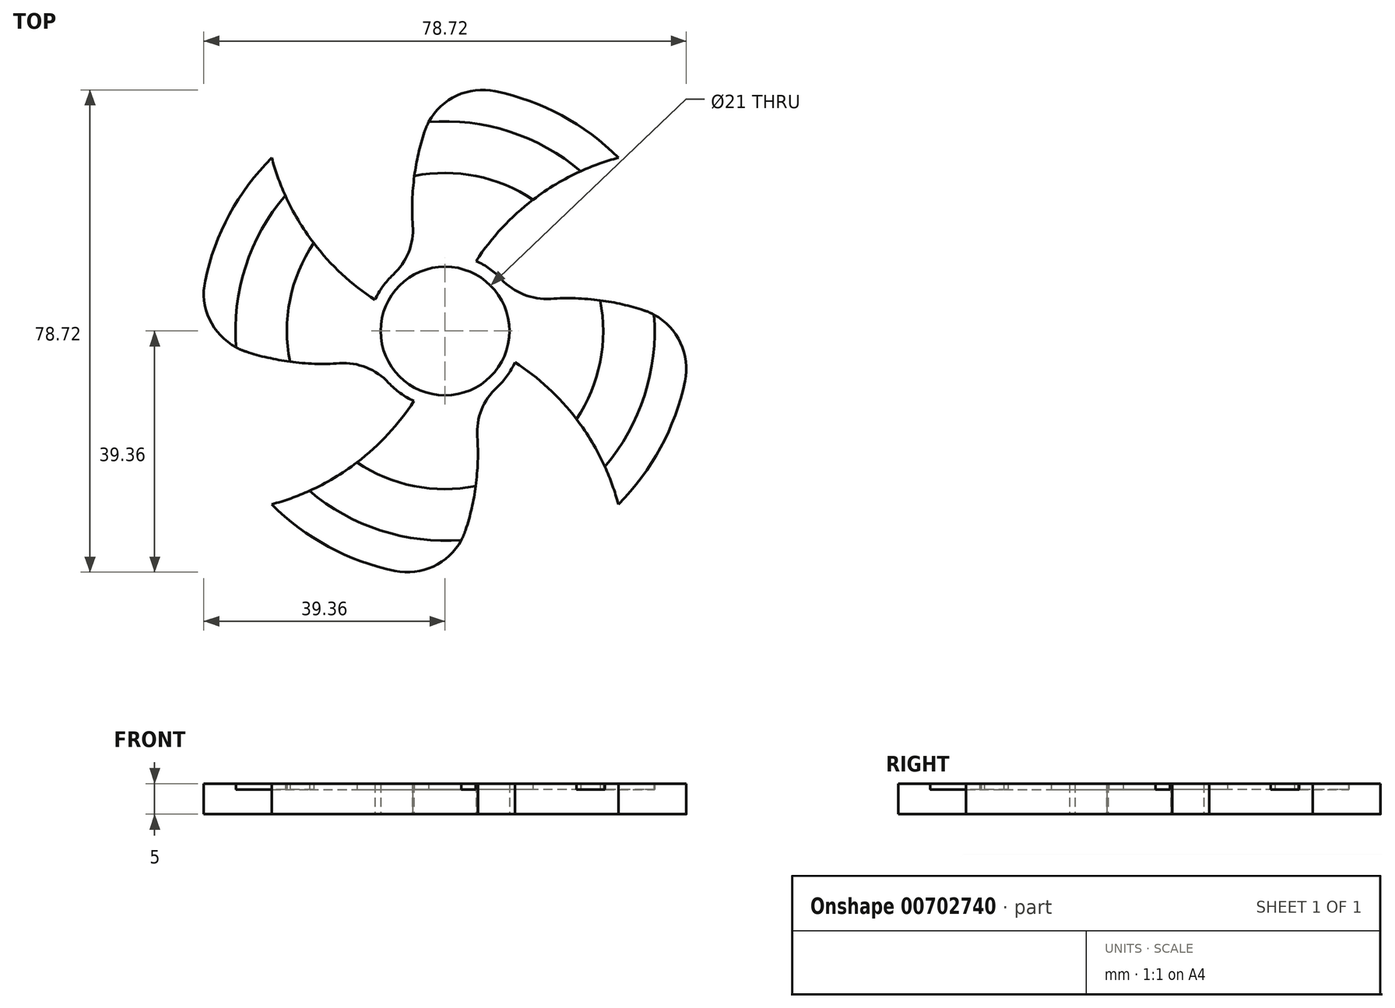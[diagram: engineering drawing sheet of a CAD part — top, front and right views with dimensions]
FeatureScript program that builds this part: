
annotation { "Feature Type Name" : "Feature", "Feature Type Description" : "" }
export const myFeature = defineFeature(function(context is Context, id is Id, definition is map)
    precondition{}
    {
        {
            var Q0;
            Q0=qCreatedBy(makeId("Top.planeOp"),FACE);
            var sketch = newSketch(context, id + "F0", { "sketchPlane" : qUnion([Q0])});
            skArc(sketch, "E0", {"start": v(28.28, 28.28) * mm, "mid": v(15.3, 36.96) * mm, "end": v(0, 40) * mm});
            skLineSegment(sketch, "E1", {"start": v(0, 0) * mm, "end": v(40, 0) * mm, "construction": true});
            skLineSegment(sketch, "E2", {"start": v(0, 0) * mm, "end": v(-40, 0) * mm, "construction": true});
            skLineSegment(sketch, "E3", {"start": v(0, 0) * mm, "end": v(-28.28, 28.28) * mm, "construction": true});
            skLineSegment(sketch, "E4", {"start": v(0, 0) * mm, "end": v(28.28, 28.28) * mm, "construction": true});
            skLineSegment(sketch, "E5", {"start": v(0, 0) * mm, "end": v(28.28, -28.28) * mm, "construction": true});
            skLineSegment(sketch, "E6", {"start": v(0, 0) * mm, "end": v(-28.28, -28.28) * mm, "construction": true});
            skLineSegment(sketch, "E7", {"start": v(0, 40) * mm, "end": v(0, -40) * mm, "construction": true});
            skArc(sketch, "E8", {"start": v(28.28, 28.28) * mm, "mid": v(15.12, 22) * mm, "end": v(5.08, 11.42) * mm});
            skArc(sketch, "E9", {"start": v(40, 0) * mm, "mid": v(26.25, 4.87) * mm, "end": v(11.67, 4.48) * mm});
            skArc(sketch, "E10", {"start": v(28.28, -28.28) * mm, "mid": v(22, -15.12) * mm, "end": v(11.42, -5.08) * mm});
            skArc(sketch, "E11", {"start": v(0, -40) * mm, "mid": v(4.87, -26.25) * mm, "end": v(4.48, -11.67) * mm});
            skArc(sketch, "E12", {"start": v(-28.28, -28.28) * mm, "mid": v(-15.12, -22) * mm, "end": v(-5.08, -11.42) * mm});
            skArc(sketch, "E13", {"start": v(-40, 0) * mm, "mid": v(-26.25, -4.87) * mm, "end": v(-11.67, -4.48) * mm});
            skArc(sketch, "E14", {"start": v(-28.28, 28.28) * mm, "mid": v(-22, 15.12) * mm, "end": v(-11.42, 5.08) * mm});
            skArc(sketch, "E15", {"start": v(0, 40) * mm, "mid": v(-4.87, 26.25) * mm, "end": v(-4.48, 11.67) * mm});
            skArc(sketch, "E16.trimOffspring", {"start": v(-28.28, -28.28) * mm, "mid": v(-15.3, -36.96) * mm, "end": v(0, -40) * mm});
            skArc(sketch, "E17.trimOffspring", {"start": v(28.28, -28.28) * mm, "mid": v(36.96, -15.3) * mm, "end": v(40, 0) * mm});
            skArc(sketch, "E18.trimOffspring", {"start": v(-28.28, 28.28) * mm, "mid": v(-36.96, 15.3) * mm, "end": v(-40, 0) * mm});
            skCircle(sketch, "E19", {"center": v(0, 0) * mm, "radius": 12.5 * mm});
            skCircle(sketch, "E20", {"center": v(0, 0) * mm, "radius": 10.5 * mm});
            skSolve(sketch);
        }
        {
            var Q0;
            {var subQ0=sQuery(id+"F0.wireOp",EDGE,"E13");Q0=makeQuery(id+"F0.imprint","IMPRINT",FACE,{"disambiguationData":[TD([[makeQuery(id+"F0.imprint","IMPRINT",EDGE,{"derivedFrom":subQ0}),1.0]])]});}
            var Q1;
            Q1=makeQuery(id+"F0.imprint","IMPRINT",FACE,{"disambiguationData":[TD([[makeQuery(id+"F0.imprint","IMPRINT",EDGE,{"derivedFrom":sQuery(id+"F0.wireOp",EDGE,"E0")}),1.0]])]});
            var Q2;
            Q2=makeQuery(id+"F0.imprint","IMPRINT",FACE,{"disambiguationData":[TD([[makeQuery(id+"F0.imprint","IMPRINT",EDGE,{"derivedFrom":sQuery(id+"F0.wireOp",EDGE,"E20")}),-1.0]])]});
            var Q3;
            {var subQ0=sQuery(id+"F0.wireOp",EDGE,"E9");Q3=makeQuery(id+"F0.imprint","IMPRINT",FACE,{"disambiguationData":[TD([[makeQuery(id+"F0.imprint","IMPRINT",EDGE,{"derivedFrom":subQ0}),1.0]])]});}
            var Q4;
            {var subQ0=sQuery(id+"F0.wireOp",EDGE,"E11");Q4=makeQuery(id+"F0.imprint","IMPRINT",FACE,{"disambiguationData":[TD([[makeQuery(id+"F0.imprint","IMPRINT",EDGE,{"derivedFrom":subQ0}),1.0]])]});}
            extrude(context, id + "F1", {"entities" : qUnion([Q0, Q1, Q2, Q3, Q4]), "depth" : 5 * mm, "offsetDistance" : 25 * mm});
        }
        {
            var Q0;
            Q0=makeQuery(id+"F1.opExtrude","SWEPT_EDGE",EDGE,{"disambiguationData":[OSD([sQuery(id+"F0.wireOp",EDGE,"E13"),sQuery(id+"F0.wireOp",EDGE,"E18.trimOffspring")])]});
            var Q1;
            Q1=makeQuery(id+"F1.opExtrude","SWEPT_EDGE",EDGE,{"disambiguationData":[OSD([sQuery(id+"F0.wireOp",EDGE,"E11"),sQuery(id+"F0.wireOp",EDGE,"E16.trimOffspring")])]});
            var Q2;
            Q2=makeQuery(id+"F1.opExtrude","SWEPT_EDGE",EDGE,{"disambiguationData":[OSD([sQuery(id+"F0.wireOp",EDGE,"E9"),sQuery(id+"F0.wireOp",EDGE,"E17.trimOffspring")])]});
            var Q3;
            Q3=makeQuery(id+"F1.opExtrude","SWEPT_EDGE",EDGE,{"disambiguationData":[OSD([sQuery(id+"F0.wireOp",EDGE,"E0"),sQuery(id+"F0.wireOp",EDGE,"E15")])]});
            fillet(context, id + "F2", {"entities" : qUnion([Q0, Q1, Q2, Q3]), "radius" : 10 * mm, "tangentPropagation" : true, "allowEdgeOverflow" : false});
        }
        {
            var Q0;
            Q0=makeQuery(id+"F1.opExtrude","CAP_FACE",FACE,{"disambiguationData":[OSD([sQuery(id+"F0.wireOp",EDGE,"E0"),sQuery(id+"F0.wireOp",EDGE,"E8"),sQuery(id+"F0.wireOp",EDGE,"E9"),sQuery(id+"F0.wireOp",EDGE,"E10"),sQuery(id+"F0.wireOp",EDGE,"E11"),sQuery(id+"F0.wireOp",EDGE,"E12"),sQuery(id+"F0.wireOp",EDGE,"E13"),sQuery(id+"F0.wireOp",EDGE,"E14"),sQuery(id+"F0.wireOp",EDGE,"E15"),sQuery(id+"F0.wireOp",EDGE,"E16.trimOffspring"),sQuery(id+"F0.wireOp",EDGE,"E17.trimOffspring"),sQuery(id+"F0.wireOp",EDGE,"E18.trimOffspring"),sQuery(id+"F0.wireOp",EDGE,"E19"),sQuery(id+"F0.wireOp",EDGE,"E20")])],"isStart":false});
            var sketch = newSketch(context, id + "F3", { "sketchPlane" : qUnion([Q0])});
            skCircle(sketch, "E21", {"center": v(0, 0) * mm, "radius": 25.8 * mm});
            skCircle(sketch, "E22", {"center": v(0, 0) * mm, "radius": 34.2 * mm});
            skSolve(sketch);
        }
        {
            var Q0;
            {var subQ3=sQuery(id+"F0.wireOp",EDGE,"E14");var subQ8=makeQuery(id+"F1.opExtrude","CAP_EDGE",EDGE,{"disambiguationData":[OSD([subQ3])],"isStart":false});var subQ10=sQuery(id+"F3.wireOp",EDGE,"E21");var subQ11=makeQuery(id+"F3.imprint","INTERSECT",VERTEX,{"derivedFrom":[subQ8,subQ10]});Q0=makeQuery(id+"F3.imprint","IMPRINT",FACE,{"disambiguationData":[TD([[makeQuery(id+"F3.imprint","IMPRINT",EDGE,{"disambiguationData":[TD([[subQ11,-1.0]])],"derivedFrom":subQ10}),-1.0]])]});}
            var Q1;
            {var subQ2=sQuery(id+"F0.wireOp",EDGE,"E8");var subQ8=makeQuery(id+"F1.opExtrude","CAP_EDGE",EDGE,{"disambiguationData":[OSD([subQ2])],"isStart":false});var subQ10=sQuery(id+"F3.wireOp",EDGE,"E21");var subQ11=makeQuery(id+"F3.imprint","INTERSECT",VERTEX,{"derivedFrom":[subQ8,subQ10]});Q1=makeQuery(id+"F3.imprint","IMPRINT",FACE,{"disambiguationData":[TD([[makeQuery(id+"F3.imprint","IMPRINT",EDGE,{"disambiguationData":[TD([[subQ11,-1.0]])],"derivedFrom":subQ10}),-1.0]])]});}
            var Q2;
            {var subQ0=sQuery(id+"F0.wireOp",EDGE,"E9");var subQ1=makeQuery(id+"F1.opExtrude","CAP_EDGE",EDGE,{"disambiguationData":[OSD([subQ0])],"isStart":false});var subQ8=sQuery(id+"F3.wireOp",EDGE,"E21");var subQ9=makeQuery(id+"F3.imprint","INTERSECT",VERTEX,{"derivedFrom":[subQ1,subQ8]});Q2=makeQuery(id+"F3.imprint","IMPRINT",FACE,{"disambiguationData":[TD([[makeQuery(id+"F3.imprint","IMPRINT",EDGE,{"disambiguationData":[TD([[subQ9,1.0]])],"derivedFrom":subQ8}),-1.0]])]});}
            var Q3;
            {var subQ3=sQuery(id+"F0.wireOp",EDGE,"E12");var subQ8=makeQuery(id+"F1.opExtrude","CAP_EDGE",EDGE,{"disambiguationData":[OSD([subQ3])],"isStart":false});var subQ10=sQuery(id+"F3.wireOp",EDGE,"E21");var subQ11=makeQuery(id+"F3.imprint","INTERSECT",VERTEX,{"derivedFrom":[subQ8,subQ10]});Q3=makeQuery(id+"F3.imprint","IMPRINT",FACE,{"disambiguationData":[TD([[makeQuery(id+"F3.imprint","IMPRINT",EDGE,{"disambiguationData":[TD([[subQ11,-1.0]])],"derivedFrom":subQ10}),-1.0]])]});}
            extrude(context, id + "F4", {"entities" : qUnion([Q0, Q1, Q2, Q3]), "operationType" : NewBodyOperationType.REMOVE, "oppositeDirection" : true, "depth" : 1 * mm, "offsetDistance" : 25 * mm});
        }
        {
            var Q0;
            {var subQ0=sQuery(id+"F0.wireOp",EDGE,"E13");var subQ1=makeQuery(id+"F1.opExtrude","CAP_EDGE",EDGE,{"disambiguationData":[OSD([subQ0])],"isStart":false});var subQ2=sQuery(id+"F0.wireOp",EDGE,"E20");var subQ3=sQuery(id+"F0.wireOp",EDGE,"E19");var subQ4=sQuery(id+"F0.wireOp",EDGE,"E18.trimOffspring");var subQ5=sQuery(id+"F0.wireOp",EDGE,"E17.trimOffspring");var subQ6=sQuery(id+"F0.wireOp",EDGE,"E16.trimOffspring");var subQ7=sQuery(id+"F0.wireOp",EDGE,"E15");var subQ8=sQuery(id+"F0.wireOp",EDGE,"E14");var subQ9=sQuery(id+"F0.wireOp",EDGE,"E12");var subQ10=sQuery(id+"F0.wireOp",EDGE,"E11");var subQ11=sQuery(id+"F0.wireOp",EDGE,"E10");var subQ12=sQuery(id+"F0.wireOp",EDGE,"E9");var subQ13=sQuery(id+"F0.wireOp",EDGE,"E8");var subQ14=sQuery(id+"F0.wireOp",EDGE,"E0");var subQ15=makeQuery(id+"F2.opFillet","BLEND_EDGE",EDGE,{"blendedFrom":[makeQuery(id+"F1.opExtrude","SWEPT_EDGE",EDGE,{"disambiguationData":[OSD([subQ0,subQ4])]}),makeQuery(id+"F1.opExtrude","CAP_FACE",FACE,{"disambiguationData":[OSD([subQ14,subQ13,subQ12,subQ11,subQ10,subQ9,subQ0,subQ8,subQ7,subQ6,subQ5,subQ4,subQ3,subQ2])],"isStart":false})],"blendedInto":[makeQuery(id+"F1.opExtrude","CAP_FACE",FACE,{"disambiguationData":[OSD([subQ14,subQ13,subQ12,subQ11,subQ10,subQ9,subQ0,subQ8,subQ7,subQ6,subQ5,subQ4,subQ3,subQ2])],"isStart":false})]});var subQ16=makeQuery(id+"F3.imprint","INTERSECT",VERTEX,{"derivedFrom":[subQ15,subQ1]});var subQ17=sQuery(id+"F3.wireOp",EDGE,"E21");var subQ18=makeQuery(id+"F3.imprint","INTERSECT",VERTEX,{"derivedFrom":[subQ1,subQ17]});var subQ19=sQuery(id+"F3.wireOp",EDGE,"E22");var subQ21=makeQuery(id+"F1.opExtrude","CAP_EDGE",EDGE,{"disambiguationData":[OSD([subQ8])],"isStart":false});var subQ22=makeQuery(id+"F3.imprint","INTERSECT",VERTEX,{"derivedFrom":[subQ21,subQ19]});var subQ23=makeQuery(id+"F3.imprint","INTERSECT",VERTEX,{"derivedFrom":[subQ21,subQ17]});Q0=makeQuery(id+"F4.boolean.opBoolean","COPY",FACE,{"derivedFrom":makeQuery(id+"F4.opExtrude","CAP_FACE",FACE,{"disambiguationData":[OSD([subQ14,subQ13,subQ12,subQ11,subQ10,subQ9,subQ0,subQ8,subQ7,subQ6,subQ5,subQ4,subQ3,subQ2,subQ17,subQ19]),TDD([makeQuery(id+"F3.imprint","IMPRINT",EDGE,{"disambiguationData":[TD([[subQ23,-1.0]])],"derivedFrom":subQ17}),makeQuery(id+"F3.imprint","IMPRINT",EDGE,{"disambiguationData":[TD([[subQ22,-1.0]])],"derivedFrom":subQ19}),makeQuery(id+"F3.imprint","IMPRINT",EDGE,{"disambiguationData":[TD([[subQ22,-1.0]])],"derivedFrom":subQ21}),makeQuery(id+"F3.imprint","IMPRINT",EDGE,{"disambiguationData":[TD([[subQ16,1.0]])],"derivedFrom":subQ15}),makeQuery(id+"F3.imprint","IMPRINT",EDGE,{"disambiguationData":[TD([[subQ18,1.0]])],"derivedFrom":subQ1})])],"isStart":false})});}
            var Q1;
            {var subQ0=sQuery(id+"F0.wireOp",EDGE,"E15");var subQ1=makeQuery(id+"F1.opExtrude","CAP_EDGE",EDGE,{"disambiguationData":[OSD([subQ0])],"isStart":false});var subQ2=sQuery(id+"F0.wireOp",EDGE,"E20");var subQ3=sQuery(id+"F0.wireOp",EDGE,"E19");var subQ4=sQuery(id+"F0.wireOp",EDGE,"E18.trimOffspring");var subQ5=sQuery(id+"F0.wireOp",EDGE,"E17.trimOffspring");var subQ6=sQuery(id+"F0.wireOp",EDGE,"E16.trimOffspring");var subQ7=sQuery(id+"F0.wireOp",EDGE,"E14");var subQ8=sQuery(id+"F0.wireOp",EDGE,"E13");var subQ9=sQuery(id+"F0.wireOp",EDGE,"E12");var subQ10=sQuery(id+"F0.wireOp",EDGE,"E11");var subQ11=sQuery(id+"F0.wireOp",EDGE,"E10");var subQ12=sQuery(id+"F0.wireOp",EDGE,"E9");var subQ13=sQuery(id+"F0.wireOp",EDGE,"E8");var subQ14=sQuery(id+"F0.wireOp",EDGE,"E0");var subQ15=makeQuery(id+"F2.opFillet","BLEND_EDGE",EDGE,{"blendedFrom":[makeQuery(id+"F1.opExtrude","SWEPT_EDGE",EDGE,{"disambiguationData":[OSD([subQ14,subQ0])]}),makeQuery(id+"F1.opExtrude","CAP_FACE",FACE,{"disambiguationData":[OSD([subQ14,subQ13,subQ12,subQ11,subQ10,subQ9,subQ8,subQ7,subQ0,subQ6,subQ5,subQ4,subQ3,subQ2])],"isStart":false})],"blendedInto":[makeQuery(id+"F1.opExtrude","CAP_FACE",FACE,{"disambiguationData":[OSD([subQ14,subQ13,subQ12,subQ11,subQ10,subQ9,subQ8,subQ7,subQ0,subQ6,subQ5,subQ4,subQ3,subQ2])],"isStart":false})]});var subQ16=makeQuery(id+"F3.imprint","INTERSECT",VERTEX,{"derivedFrom":[subQ15,subQ1]});var subQ17=sQuery(id+"F3.wireOp",EDGE,"E21");var subQ18=makeQuery(id+"F3.imprint","INTERSECT",VERTEX,{"derivedFrom":[subQ1,subQ17]});var subQ19=sQuery(id+"F3.wireOp",EDGE,"E22");var subQ21=makeQuery(id+"F1.opExtrude","CAP_EDGE",EDGE,{"disambiguationData":[OSD([subQ13])],"isStart":false});var subQ22=makeQuery(id+"F3.imprint","INTERSECT",VERTEX,{"derivedFrom":[subQ21,subQ19]});var subQ23=makeQuery(id+"F3.imprint","INTERSECT",VERTEX,{"derivedFrom":[subQ21,subQ17]});Q1=makeQuery(id+"F4.boolean.opBoolean","COPY",FACE,{"derivedFrom":makeQuery(id+"F4.opExtrude","CAP_FACE",FACE,{"disambiguationData":[OSD([subQ14,subQ13,subQ12,subQ11,subQ10,subQ9,subQ8,subQ7,subQ0,subQ6,subQ5,subQ4,subQ3,subQ2,subQ17,subQ19]),TDD([makeQuery(id+"F3.imprint","IMPRINT",EDGE,{"disambiguationData":[TD([[subQ23,-1.0]])],"derivedFrom":subQ17}),makeQuery(id+"F3.imprint","IMPRINT",EDGE,{"disambiguationData":[TD([[subQ22,-1.0]])],"derivedFrom":subQ19}),makeQuery(id+"F3.imprint","IMPRINT",EDGE,{"disambiguationData":[TD([[subQ22,-1.0]])],"derivedFrom":subQ21}),makeQuery(id+"F3.imprint","IMPRINT",EDGE,{"disambiguationData":[TD([[subQ16,1.0]])],"derivedFrom":subQ15}),makeQuery(id+"F3.imprint","IMPRINT",EDGE,{"disambiguationData":[TD([[subQ18,1.0]])],"derivedFrom":subQ1})])],"isStart":false})});}
            var Q2;
            {var subQ0=sQuery(id+"F0.wireOp",EDGE,"E9");var subQ1=makeQuery(id+"F1.opExtrude","CAP_EDGE",EDGE,{"disambiguationData":[OSD([subQ0])],"isStart":false});var subQ2=sQuery(id+"F0.wireOp",EDGE,"E20");var subQ3=sQuery(id+"F0.wireOp",EDGE,"E19");var subQ4=sQuery(id+"F0.wireOp",EDGE,"E18.trimOffspring");var subQ5=sQuery(id+"F0.wireOp",EDGE,"E17.trimOffspring");var subQ6=sQuery(id+"F0.wireOp",EDGE,"E16.trimOffspring");var subQ7=sQuery(id+"F0.wireOp",EDGE,"E15");var subQ8=sQuery(id+"F0.wireOp",EDGE,"E14");var subQ9=sQuery(id+"F0.wireOp",EDGE,"E13");var subQ10=sQuery(id+"F0.wireOp",EDGE,"E12");var subQ11=sQuery(id+"F0.wireOp",EDGE,"E11");var subQ12=sQuery(id+"F0.wireOp",EDGE,"E10");var subQ13=sQuery(id+"F0.wireOp",EDGE,"E8");var subQ14=sQuery(id+"F0.wireOp",EDGE,"E0");var subQ15=makeQuery(id+"F2.opFillet","BLEND_EDGE",EDGE,{"blendedFrom":[makeQuery(id+"F1.opExtrude","SWEPT_EDGE",EDGE,{"disambiguationData":[OSD([subQ0,subQ5])]}),makeQuery(id+"F1.opExtrude","CAP_FACE",FACE,{"disambiguationData":[OSD([subQ14,subQ13,subQ0,subQ12,subQ11,subQ10,subQ9,subQ8,subQ7,subQ6,subQ5,subQ4,subQ3,subQ2])],"isStart":false})],"blendedInto":[makeQuery(id+"F1.opExtrude","CAP_FACE",FACE,{"disambiguationData":[OSD([subQ14,subQ13,subQ0,subQ12,subQ11,subQ10,subQ9,subQ8,subQ7,subQ6,subQ5,subQ4,subQ3,subQ2])],"isStart":false})]});var subQ16=makeQuery(id+"F3.imprint","INTERSECT",VERTEX,{"derivedFrom":[subQ15,subQ1]});var subQ17=sQuery(id+"F3.wireOp",EDGE,"E21");var subQ18=makeQuery(id+"F3.imprint","INTERSECT",VERTEX,{"derivedFrom":[subQ1,subQ17]});var subQ19=sQuery(id+"F3.wireOp",EDGE,"E22");var subQ21=makeQuery(id+"F1.opExtrude","CAP_EDGE",EDGE,{"disambiguationData":[OSD([subQ12])],"isStart":false});var subQ22=makeQuery(id+"F3.imprint","INTERSECT",VERTEX,{"derivedFrom":[subQ21,subQ19]});Q2=makeQuery(id+"F4.boolean.opBoolean","COPY",FACE,{"derivedFrom":makeQuery(id+"F4.opExtrude","CAP_FACE",FACE,{"disambiguationData":[OSD([subQ14,subQ13,subQ0,subQ12,subQ11,subQ10,subQ9,subQ8,subQ7,subQ6,subQ5,subQ4,subQ3,subQ2,subQ17,subQ19]),TDD([makeQuery(id+"F3.imprint","IMPRINT",EDGE,{"disambiguationData":[TD([[subQ18,1.0]])],"derivedFrom":subQ17}),makeQuery(id+"F3.imprint","IMPRINT",EDGE,{"disambiguationData":[TD([[subQ22,-1.0]])],"derivedFrom":subQ19}),makeQuery(id+"F3.imprint","IMPRINT",EDGE,{"disambiguationData":[TD([[subQ22,-1.0]])],"derivedFrom":subQ21}),makeQuery(id+"F3.imprint","IMPRINT",EDGE,{"disambiguationData":[TD([[subQ16,1.0]])],"derivedFrom":subQ15}),makeQuery(id+"F3.imprint","IMPRINT",EDGE,{"disambiguationData":[TD([[subQ18,1.0]])],"derivedFrom":subQ1})])],"isStart":false})});}
            var Q3;
            {var subQ0=sQuery(id+"F0.wireOp",EDGE,"E11");var subQ1=makeQuery(id+"F1.opExtrude","CAP_EDGE",EDGE,{"disambiguationData":[OSD([subQ0])],"isStart":false});var subQ2=sQuery(id+"F0.wireOp",EDGE,"E20");var subQ3=sQuery(id+"F0.wireOp",EDGE,"E19");var subQ4=sQuery(id+"F0.wireOp",EDGE,"E18.trimOffspring");var subQ5=sQuery(id+"F0.wireOp",EDGE,"E17.trimOffspring");var subQ6=sQuery(id+"F0.wireOp",EDGE,"E16.trimOffspring");var subQ7=sQuery(id+"F0.wireOp",EDGE,"E15");var subQ8=sQuery(id+"F0.wireOp",EDGE,"E14");var subQ9=sQuery(id+"F0.wireOp",EDGE,"E13");var subQ10=sQuery(id+"F0.wireOp",EDGE,"E12");var subQ11=sQuery(id+"F0.wireOp",EDGE,"E10");var subQ12=sQuery(id+"F0.wireOp",EDGE,"E9");var subQ13=sQuery(id+"F0.wireOp",EDGE,"E8");var subQ14=sQuery(id+"F0.wireOp",EDGE,"E0");var subQ15=makeQuery(id+"F2.opFillet","BLEND_EDGE",EDGE,{"blendedFrom":[makeQuery(id+"F1.opExtrude","SWEPT_EDGE",EDGE,{"disambiguationData":[OSD([subQ0,subQ6])]}),makeQuery(id+"F1.opExtrude","CAP_FACE",FACE,{"disambiguationData":[OSD([subQ14,subQ13,subQ12,subQ11,subQ0,subQ10,subQ9,subQ8,subQ7,subQ6,subQ5,subQ4,subQ3,subQ2])],"isStart":false})],"blendedInto":[makeQuery(id+"F1.opExtrude","CAP_FACE",FACE,{"disambiguationData":[OSD([subQ14,subQ13,subQ12,subQ11,subQ0,subQ10,subQ9,subQ8,subQ7,subQ6,subQ5,subQ4,subQ3,subQ2])],"isStart":false})]});var subQ16=makeQuery(id+"F3.imprint","INTERSECT",VERTEX,{"derivedFrom":[subQ15,subQ1]});var subQ17=sQuery(id+"F3.wireOp",EDGE,"E21");var subQ18=makeQuery(id+"F3.imprint","INTERSECT",VERTEX,{"derivedFrom":[subQ1,subQ17]});var subQ19=sQuery(id+"F3.wireOp",EDGE,"E22");var subQ21=makeQuery(id+"F1.opExtrude","CAP_EDGE",EDGE,{"disambiguationData":[OSD([subQ10])],"isStart":false});var subQ22=makeQuery(id+"F3.imprint","INTERSECT",VERTEX,{"derivedFrom":[subQ21,subQ19]});var subQ23=makeQuery(id+"F3.imprint","INTERSECT",VERTEX,{"derivedFrom":[subQ21,subQ17]});Q3=makeQuery(id+"F4.boolean.opBoolean","COPY",FACE,{"derivedFrom":makeQuery(id+"F4.opExtrude","CAP_FACE",FACE,{"disambiguationData":[OSD([subQ14,subQ13,subQ12,subQ11,subQ0,subQ10,subQ9,subQ8,subQ7,subQ6,subQ5,subQ4,subQ3,subQ2,subQ17,subQ19]),TDD([makeQuery(id+"F3.imprint","IMPRINT",EDGE,{"disambiguationData":[TD([[subQ23,-1.0]])],"derivedFrom":subQ17}),makeQuery(id+"F3.imprint","IMPRINT",EDGE,{"disambiguationData":[TD([[subQ22,-1.0]])],"derivedFrom":subQ19}),makeQuery(id+"F3.imprint","IMPRINT",EDGE,{"disambiguationData":[TD([[subQ22,-1.0]])],"derivedFrom":subQ21}),makeQuery(id+"F3.imprint","IMPRINT",EDGE,{"disambiguationData":[TD([[subQ16,1.0]])],"derivedFrom":subQ15}),makeQuery(id+"F3.imprint","IMPRINT",EDGE,{"disambiguationData":[TD([[subQ18,1.0]])],"derivedFrom":subQ1})])],"isStart":false})});}
            var Q4;
            {var subQ0=sQuery(id+"F0.wireOp",EDGE,"E12");var subQ1=sQuery(id+"F0.wireOp",EDGE,"E16.trimOffspring");var subQ2=sQuery(id+"F0.wireOp",EDGE,"E11");var subQ4=makeQuery(id+"F1.opExtrude","CAP_FACE",FACE,{"disambiguationData":[OSD([sQuery(id+"F0.wireOp",EDGE,"E0"),sQuery(id+"F0.wireOp",EDGE,"E8"),sQuery(id+"F0.wireOp",EDGE,"E9"),sQuery(id+"F0.wireOp",EDGE,"E10"),subQ2,subQ0,sQuery(id+"F0.wireOp",EDGE,"E13"),sQuery(id+"F0.wireOp",EDGE,"E14"),sQuery(id+"F0.wireOp",EDGE,"E15"),subQ1,sQuery(id+"F0.wireOp",EDGE,"E17.trimOffspring"),sQuery(id+"F0.wireOp",EDGE,"E18.trimOffspring"),sQuery(id+"F0.wireOp",EDGE,"E19"),sQuery(id+"F0.wireOp",EDGE,"E20")])],"isStart":false});Q4=makeQuery(id+"F4.boolean.opBoolean","SPLIT",FACE,{"disambiguationData":[TD([makeQuery(id+"F1.opExtrude","SWEPT_FACE",FACE,{"disambiguationData":[OSD([subQ1])]})])],"derivedFrom":subQ4});}
            extrude(context, id + "F5", {"entities" : qUnion([Q0, Q1, Q2, Q3]), "endBound" : BoundingType.UP_TO_SURFACE, "depth" : 25 * mm, "endBoundEntityFace" : qUnion([Q4]), "offsetDistance" : 25 * mm});
        }
        {
            var Q0;
            Q0=makeQuery(id+"F0.imprint","IMPRINT",FACE,{"disambiguationData":[TD([[makeQuery(id+"F0.imprint","IMPRINT",EDGE,{"derivedFrom":sQuery(id+"F0.wireOp",EDGE,"E20")}),1.0]])]});
            var Q1;
            {var subQ0=sQuery(id+"F0.wireOp",EDGE,"E15");var subQ1=sQuery(id+"F0.wireOp",EDGE,"E14");var subQ2=sQuery(id+"F0.wireOp",EDGE,"E13");var subQ3=sQuery(id+"F0.wireOp",EDGE,"E12");var subQ4=sQuery(id+"F0.wireOp",EDGE,"E19");var subQ5=sQuery(id+"F0.wireOp",EDGE,"E8");var subQ6=sQuery(id+"F0.wireOp",EDGE,"E9");var subQ7=sQuery(id+"F0.wireOp",EDGE,"E10");var subQ8=sQuery(id+"F0.wireOp",EDGE,"E11");var subQ10=sQuery(id+"F0.wireOp",EDGE,"E20");Q1=makeQuery(id+"F4.boolean.opBoolean","SPLIT",FACE,{"disambiguationData":[TD([makeQuery(id+"F1.opExtrude","SWEPT_FACE",FACE,{"disambiguationData":[OSD([subQ6])]})])],"derivedFrom":makeQuery(id+"F1.opExtrude","CAP_FACE",FACE,{"disambiguationData":[OSD([sQuery(id+"F0.wireOp",EDGE,"E0"),subQ5,subQ6,subQ7,subQ8,subQ3,subQ2,subQ1,subQ0,sQuery(id+"F0.wireOp",EDGE,"E16.trimOffspring"),sQuery(id+"F0.wireOp",EDGE,"E17.trimOffspring"),sQuery(id+"F0.wireOp",EDGE,"E18.trimOffspring"),subQ4,subQ10])],"isStart":false})});}
            extrude(context, id + "F6", {"entities" : qUnion([Q0]), "endBound" : BoundingType.UP_TO_SURFACE, "depth" : 25 * mm, "endBoundEntityFace" : qUnion([Q1]), "offsetDistance" : 25 * mm});
        }
        {
            var Q0;
            Q0=makeQuery(id+"F1.opExtrude","SWEPT_EDGE",EDGE,{"disambiguationData":[OSD([sQuery(id+"F0.wireOp",EDGE,"E13"),sQuery(id+"F0.wireOp",EDGE,"E19")])]});
            var Q1;
            Q1=makeQuery(id+"F1.opExtrude","SWEPT_EDGE",EDGE,{"disambiguationData":[OSD([sQuery(id+"F0.wireOp",EDGE,"E11"),sQuery(id+"F0.wireOp",EDGE,"E19")])]});
            var Q2;
            Q2=makeQuery(id+"F1.opExtrude","SWEPT_EDGE",EDGE,{"disambiguationData":[OSD([sQuery(id+"F0.wireOp",EDGE,"E9"),sQuery(id+"F0.wireOp",EDGE,"E19")])]});
            var Q3;
            Q3=makeQuery(id+"F1.opExtrude","SWEPT_EDGE",EDGE,{"disambiguationData":[OSD([sQuery(id+"F0.wireOp",EDGE,"E15"),sQuery(id+"F0.wireOp",EDGE,"E19")])]});
            fillet(context, id + "F7", {"entities" : qUnion([Q0, Q1, Q2, Q3]), "radius" : 10 * mm, "tangentPropagation" : true, "allowEdgeOverflow" : false});
        }
    });
